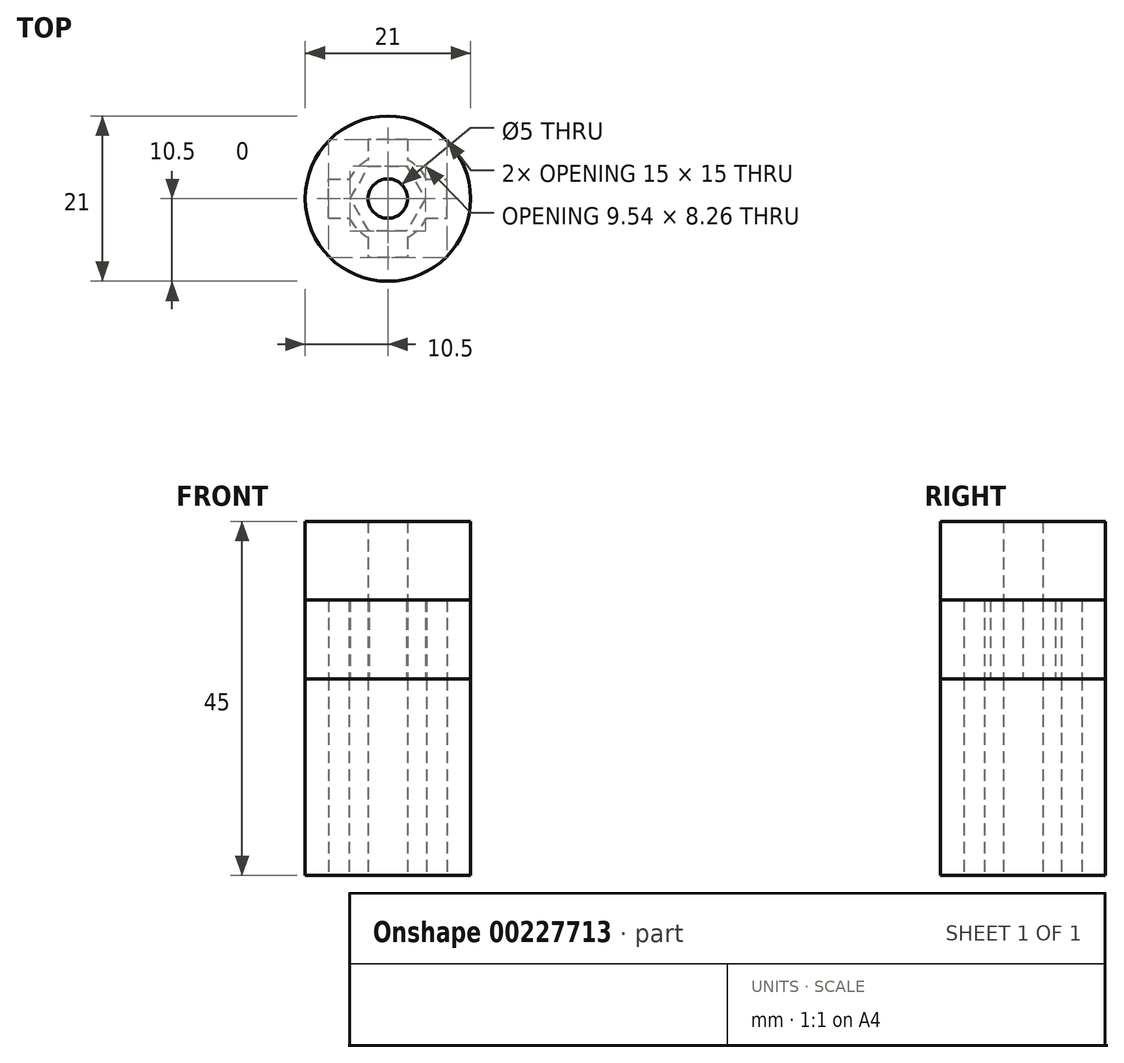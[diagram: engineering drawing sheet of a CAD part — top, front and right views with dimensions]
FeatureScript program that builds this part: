
annotation { "Feature Type Name" : "Feature", "Feature Type Description" : "" }
export const myFeature = defineFeature(function(context is Context, id is Id, definition is map)
    precondition{}
    {
        {
            var Q0;
            Q0=qCreatedBy(makeId("Top.planeOp"),FACE);
            var sketch = newSketch(context, id + "F0", { "sketchPlane" : qUnion([Q0])});
            skCircle(sketch, "E0", {"center": v(0, 0) * mm, "radius": 10.5 * mm});
            skArc(sketch, "E1", {"start": v(-4.9, -2.5) * mm, "mid": v(-3.89, -3.89) * mm, "end": v(-2.5, -4.9) * mm});
            skLineSegment(sketch, "E2.bottom", {"start": v(2.5, 7.5) * mm, "end": v(-2.5, 7.5) * mm});
            skLineSegment(sketch, "E2.top", {"start": v(2.5, -7.5) * mm, "end": v(-2.5, -7.5) * mm});
            skLineSegment(sketch, "E2.left", {"start": v(2.5, 7.5) * mm, "end": v(2.5, 4.9) * mm});
            skLineSegment(sketch, "E2.right", {"start": v(-2.5, 7.5) * mm, "end": v(-2.5, 4.9) * mm});
            skLineSegment(sketch, "E3.bottom", {"start": v(-7.5, -2.5) * mm, "end": v(-4.9, -2.5) * mm});
            skLineSegment(sketch, "E3.top", {"start": v(-7.5, 2.5) * mm, "end": v(-4.9, 2.5) * mm});
            skLineSegment(sketch, "E3.left", {"start": v(-7.5, -2.5) * mm, "end": v(-7.5, 2.5) * mm});
            skLineSegment(sketch, "E3.right", {"start": v(7.5, -2.5) * mm, "end": v(7.5, 2.5) * mm});
            skLineSegment(sketch, "E4.trimOffspring", {"start": v(2.5, -4.9) * mm, "end": v(2.5, -7.5) * mm});
            skArc(sketch, "E5.trimOffspring", {"start": v(4.9, 2.5) * mm, "mid": v(3.89, 3.89) * mm, "end": v(2.5, 4.9) * mm});
            skLineSegment(sketch, "E6.trimOffspring", {"start": v(4.9, 2.5) * mm, "end": v(7.5, 2.5) * mm});
            skArc(sketch, "E7.trimOffspring", {"start": v(-2.5, 4.9) * mm, "mid": v(-3.89, 3.89) * mm, "end": v(-4.9, 2.5) * mm});
            skArc(sketch, "E8.trimOffspring", {"start": v(2.5, -4.9) * mm, "mid": v(3.89, -3.89) * mm, "end": v(4.9, -2.5) * mm});
            skLineSegment(sketch, "E9.trimOffspring", {"start": v(4.9, -2.5) * mm, "end": v(7.5, -2.5) * mm});
            skLineSegment(sketch, "E10.trimOffspring", {"start": v(-2.5, -4.9) * mm, "end": v(-2.5, -7.5) * mm});
            skSolve(sketch);
        }
        {
            var Q0;
            Q0=makeQuery(id+"F0.imprint","IMPRINT",FACE,{"disambiguationData":[TD([[makeQuery(id+"F0.imprint","IMPRINT",EDGE,{"derivedFrom":sQuery(id+"F0.wireOp",EDGE,"E0")}),1.0]])]});
            extrude(context, id + "F1", {"entities" : qUnion([Q0]), "depth" : 25 * mm});
        }
        {
            var Q0;
            Q0=makeQuery(id+"F1.opExtrude","CAP_FACE",FACE,{"disambiguationData":[OSD([sQuery(id+"F0.wireOp",EDGE,"E0"),sQuery(id+"F0.wireOp",EDGE,"E1"),sQuery(id+"F0.wireOp",EDGE,"E2.bottom"),sQuery(id+"F0.wireOp",EDGE,"E2.top"),sQuery(id+"F0.wireOp",EDGE,"E2.left"),sQuery(id+"F0.wireOp",EDGE,"E2.right"),sQuery(id+"F0.wireOp",EDGE,"E3.bottom"),sQuery(id+"F0.wireOp",EDGE,"E3.top"),sQuery(id+"F0.wireOp",EDGE,"E3.left"),sQuery(id+"F0.wireOp",EDGE,"E3.right"),sQuery(id+"F0.wireOp",EDGE,"E4.trimOffspring"),sQuery(id+"F0.wireOp",EDGE,"E5.trimOffspring"),sQuery(id+"F0.wireOp",EDGE,"E6.trimOffspring"),sQuery(id+"F0.wireOp",EDGE,"E7.trimOffspring"),sQuery(id+"F0.wireOp",EDGE,"E8.trimOffspring"),sQuery(id+"F0.wireOp",EDGE,"E9.trimOffspring"),sQuery(id+"F0.wireOp",EDGE,"E10.trimOffspring")])],"isStart":false});
            var sketch = newSketch(context, id + "F2", { "sketchPlane" : qUnion([Q0])});
            skCircle(sketch, "E11", {"center": v(0, 0) * mm, "radius": 10.5 * mm});
            skPoint(sketch, "E11.first.point", {"position": v(-6.21, 8.47) * mm});
            skPoint(sketch, "E11.second.point", {"position": v(6.57, -8.2) * mm});
            skPoint(sketch, "E11.third.point", {"position": v(10.5, 0) * mm});
            skCircle(sketch, "E12.cCircle", {"center": v(0, 0) * mm, "radius": 4.13 * mm, "construction": true});
            skLineSegment(sketch, "E12.0", {"start": v(2.38, -4.13) * mm, "end": v(-2.38, -4.13) * mm});
            skLineSegment(sketch, "E12.1", {"start": v(-2.38, -4.13) * mm, "end": v(-4.77, 0) * mm});
            skLineSegment(sketch, "E12.2", {"start": v(-4.77, 0) * mm, "end": v(-2.38, 4.13) * mm});
            skLineSegment(sketch, "E12.3", {"start": v(-2.38, 4.13) * mm, "end": v(2.38, 4.13) * mm});
            skLineSegment(sketch, "E12.4", {"start": v(2.38, 4.13) * mm, "end": v(4.77, 0) * mm});
            skLineSegment(sketch, "E12.5", {"start": v(4.77, 0) * mm, "end": v(2.38, -4.13) * mm});
            skPoint(sketch, "E12.0.midPoint", {"position": v(0, -4.13) * mm});
            skSolve(sketch);
        }
        {
            var Q0;
            Q0=makeQuery(id+"F2.imprint","IMPRINT",FACE,{"disambiguationData":[TD([[makeQuery(id+"F2.imprint","IMPRINT",EDGE,{"derivedFrom":sQuery(id+"F2.wireOp",EDGE,"E12.0")}),1.0]])]});
            extrude(context, id + "F3", {"entities" : qUnion([Q0]), "depth" : 10 * mm});
        }
        {
            var Q0;
            Q0=makeQuery(id+"F1.opExtrude","CAP_FACE",FACE,{"disambiguationData":[OSD([sQuery(id+"F0.wireOp",EDGE,"E0"),sQuery(id+"F0.wireOp",EDGE,"E1"),sQuery(id+"F0.wireOp",EDGE,"E2.bottom"),sQuery(id+"F0.wireOp",EDGE,"E2.top"),sQuery(id+"F0.wireOp",EDGE,"E2.left"),sQuery(id+"F0.wireOp",EDGE,"E2.right"),sQuery(id+"F0.wireOp",EDGE,"E3.bottom"),sQuery(id+"F0.wireOp",EDGE,"E3.top"),sQuery(id+"F0.wireOp",EDGE,"E3.left"),sQuery(id+"F0.wireOp",EDGE,"E3.right"),sQuery(id+"F0.wireOp",EDGE,"E4.trimOffspring"),sQuery(id+"F0.wireOp",EDGE,"E5.trimOffspring"),sQuery(id+"F0.wireOp",EDGE,"E6.trimOffspring"),sQuery(id+"F0.wireOp",EDGE,"E7.trimOffspring"),sQuery(id+"F0.wireOp",EDGE,"E8.trimOffspring"),sQuery(id+"F0.wireOp",EDGE,"E9.trimOffspring"),sQuery(id+"F0.wireOp",EDGE,"E10.trimOffspring")])],"isStart":false});
            extrude(context, id + "F4", {"entities" : qUnion([Q0]), "depth" : 10 * mm});
        }
        {
            var Q0;
            Q0=makeQuery(id+"F4.opExtrude","CAP_FACE",FACE,{"disambiguationData":[OSD([sQuery(id+"F0.wireOp",EDGE,"E0"),sQuery(id+"F0.wireOp",EDGE,"E1"),sQuery(id+"F0.wireOp",EDGE,"E2.bottom"),sQuery(id+"F0.wireOp",EDGE,"E2.top"),sQuery(id+"F0.wireOp",EDGE,"E2.left"),sQuery(id+"F0.wireOp",EDGE,"E2.right"),sQuery(id+"F0.wireOp",EDGE,"E3.bottom"),sQuery(id+"F0.wireOp",EDGE,"E3.top"),sQuery(id+"F0.wireOp",EDGE,"E3.left"),sQuery(id+"F0.wireOp",EDGE,"E3.right"),sQuery(id+"F0.wireOp",EDGE,"E4.trimOffspring"),sQuery(id+"F0.wireOp",EDGE,"E5.trimOffspring"),sQuery(id+"F0.wireOp",EDGE,"E6.trimOffspring"),sQuery(id+"F0.wireOp",EDGE,"E7.trimOffspring"),sQuery(id+"F0.wireOp",EDGE,"E8.trimOffspring"),sQuery(id+"F0.wireOp",EDGE,"E9.trimOffspring"),sQuery(id+"F0.wireOp",EDGE,"E10.trimOffspring")])],"isStart":false});
            var sketch = newSketch(context, id + "F5", { "sketchPlane" : qUnion([Q0])});
            skCircle(sketch, "E13", {"center": v(0, 0) * mm, "radius": 10.5 * mm});
            skPoint(sketch, "E13.first.point", {"position": v(-3.28, 9.98) * mm});
            skPoint(sketch, "E13.second.point", {"position": v(3.63, -9.85) * mm});
            skPoint(sketch, "E13.third.point", {"position": v(-7.35, -7.5) * mm});
            skPoint(sketch, "E13.third.point.positionSnap0", {"position": v(0, -7.5) * mm});
            skCircle(sketch, "E14", {"center": v(0, 0) * mm, "radius": 2.5 * mm});
            skSolve(sketch);
        }
        {
            var Q0;
            Q0=makeQuery(id+"F5.imprint","IMPRINT",FACE,{"disambiguationData":[TD([[makeQuery(id+"F5.imprint","IMPRINT",EDGE,{"derivedFrom":sQuery(id+"F5.wireOp",EDGE,"E13")}),1.0]])]});
            var Q1;
            Q1=makeQuery(id+"F5.imprint","IMPRINT",FACE,{"disambiguationData":[TD([[makeQuery(id+"F5.imprint","IMPRINT",EDGE,{"derivedFrom":sQuery(id+"F5.wireOp",EDGE,"E14")}),-1.0]])]});
            extrude(context, id + "F6", {"entities" : qUnion([Q0, Q1]), "depth" : 10 * mm});
        }
    });
